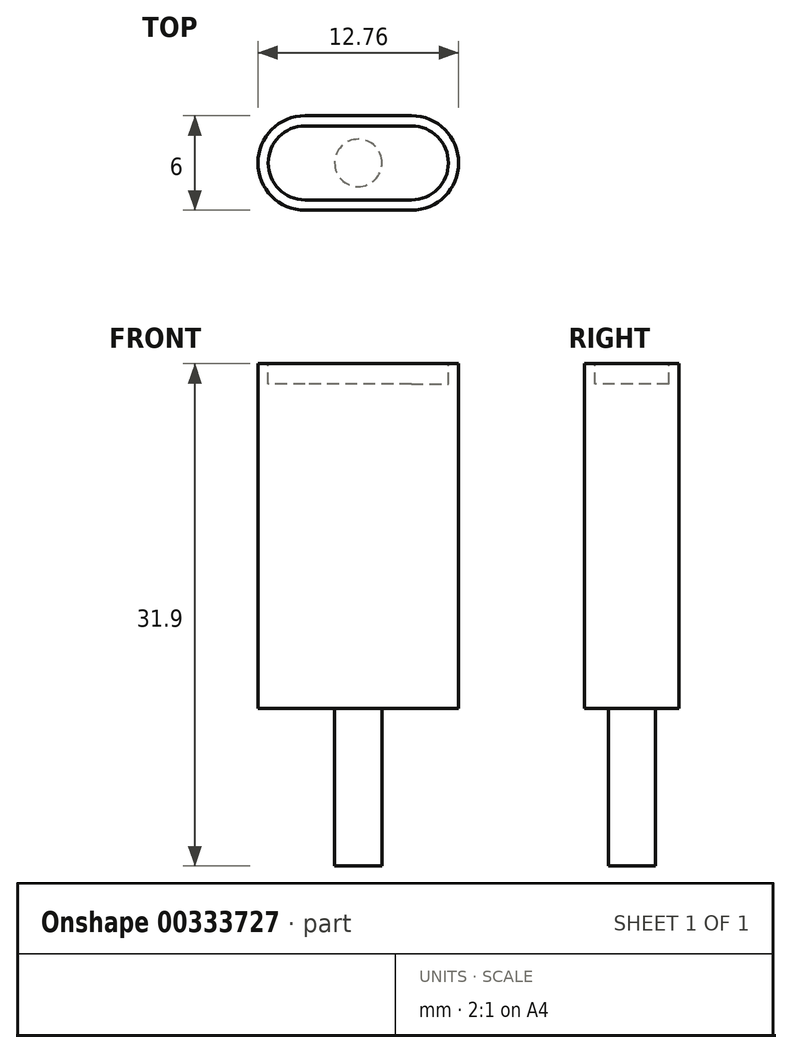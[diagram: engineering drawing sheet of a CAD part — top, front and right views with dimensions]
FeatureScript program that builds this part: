
annotation { "Feature Type Name" : "Feature", "Feature Type Description" : "" }
export const myFeature = defineFeature(function(context is Context, id is Id, definition is map)
    precondition{}
    {
        {
            var Q0;
            Q0=qCreatedBy(makeId("Top.planeOp"),FACE);
            var sketch = newSketch(context, id + "F0", { "sketchPlane" : qUnion([Q0])});
            skLineSegment(sketch, "E0.bottom", {"start": v(6.38, 3) * mm, "end": v(-6.38, 3) * mm});
            skLineSegment(sketch, "E0.top", {"start": v(6.37, -3) * mm, "end": v(-6.38, -3) * mm});
            skLineSegment(sketch, "E0.left", {"start": v(6.38, 3) * mm, "end": v(6.37, -3) * mm});
            skLineSegment(sketch, "E0.right", {"start": v(-6.38, 3) * mm, "end": v(-6.38, -3) * mm});
            skPoint(sketch, "E0.middle", {"position": v(0, 0) * mm});
            skSolve(sketch);
        }
        {
            var Q0;
            Q0=makeQuery(id+"F0.imprint","IMPRINT",FACE,{"disambiguationData":[TD([[makeQuery(id+"F0.imprint","IMPRINT",EDGE,{"derivedFrom":sQuery(id+"F0.wireOp",EDGE,"E0.bottom")}),1.0]])]});
            extrude(context, id + "F1", {"entities" : qUnion([Q0]), "depth" : 21.9 * mm});
        }
        {
            var Q0;
            Q0=makeQuery(id+"F1.opExtrude","SWEPT_EDGE",EDGE,{"disambiguationData":[OSD([sQuery(id+"F0.wireOp",EDGE,"E0.top"),sQuery(id+"F0.wireOp",EDGE,"E0.right")])]});
            var Q1;
            Q1=makeQuery(id+"F1.opExtrude","SWEPT_EDGE",EDGE,{"disambiguationData":[OSD([sQuery(id+"F0.wireOp",EDGE,"E0.bottom"),sQuery(id+"F0.wireOp",EDGE,"E0.right")])]});
            var Q2;
            Q2=makeQuery(id+"F1.opExtrude","SWEPT_EDGE",EDGE,{"disambiguationData":[OSD([sQuery(id+"F0.wireOp",EDGE,"E0.top"),sQuery(id+"F0.wireOp",EDGE,"E0.left")])]});
            var Q3;
            Q3=makeQuery(id+"F1.opExtrude","SWEPT_EDGE",EDGE,{"disambiguationData":[OSD([sQuery(id+"F0.wireOp",EDGE,"E0.bottom"),sQuery(id+"F0.wireOp",EDGE,"E0.left")])]});
            fillet(context, id + "F2", {"entities" : qUnion([Q0, Q1, Q2, Q3]), "radius" : 3 * mm, "tangentPropagation" : true, "allowEdgeOverflow" : false});
        }
        {
            var Q0;
            Q0=makeQuery(id+"F1.opExtrude","CAP_FACE",FACE,{"disambiguationData":[OSD([sQuery(id+"F0.wireOp",EDGE,"E0.bottom"),sQuery(id+"F0.wireOp",EDGE,"E0.top"),sQuery(id+"F0.wireOp",EDGE,"E0.left"),sQuery(id+"F0.wireOp",EDGE,"E0.right")])],"isStart":true});
            var sketch = newSketch(context, id + "F3", { "sketchPlane" : qUnion([Q0])});
            skCircle(sketch, "E1", {"center": v(0, 0) * mm, "radius": 1.5 * mm});
            skSolve(sketch);
        }
        {
            var Q0;
            Q0=makeQuery(id+"F3.imprint","IMPRINT",FACE,{"disambiguationData":[TD([[makeQuery(id+"F3.imprint","IMPRINT",EDGE,{"derivedFrom":sQuery(id+"F3.wireOp",EDGE,"E1")}),1.0]])]});
            extrude(context, id + "F4", {"entities" : qUnion([Q0]), "operationType" : NewBodyOperationType.ADD, "depth" : 10 * mm});
        }
        {
            var Q0;
            Q0=makeQuery(id+"F1.opExtrude","CAP_FACE",FACE,{"disambiguationData":[OSD([sQuery(id+"F0.wireOp",EDGE,"E0.bottom"),sQuery(id+"F0.wireOp",EDGE,"E0.top"),sQuery(id+"F0.wireOp",EDGE,"E0.left"),sQuery(id+"F0.wireOp",EDGE,"E0.right")])],"isStart":false});
            var sketch = newSketch(context, id + "F5", { "sketchPlane" : qUnion([Q0])});
            skLineSegment(sketch, "E2.0.0", {"start": v(-3.38, -3) * mm, "end": v(3.37, -3) * mm});
            skArc(sketch, "E2.0.1", {"start": v(3.37, -3) * mm, "mid": v(6.38, 0) * mm, "end": v(3.38, 3) * mm});
            skLineSegment(sketch, "E2.0.2", {"start": v(3.37, 3) * mm, "end": v(-3.38, 3) * mm});
            skArc(sketch, "E2.0.3", {"start": v(-3.38, 3) * mm, "mid": v(-6.38, 0) * mm, "end": v(-3.38, -3) * mm});
            skArc(sketch, "E3.0", {"start": v(-3.38, 2.35) * mm, "mid": v(-5.73, 0) * mm, "end": v(-3.38, -2.35) * mm});
            skLineSegment(sketch, "E3.1", {"start": v(3.37, 2.35) * mm, "end": v(-3.38, 2.35) * mm});
            skArc(sketch, "E3.2", {"start": v(3.38, -2.35) * mm, "mid": v(5.72, 0) * mm, "end": v(3.37, 2.35) * mm});
            skLineSegment(sketch, "E3.3", {"start": v(-3.38, -2.35) * mm, "end": v(3.37, -2.35) * mm});
            skSolve(sketch);
        }
        {
            var Q0;
            Q0=makeQuery(id+"F5.imprint","IMPRINT",FACE,{"disambiguationData":[TD([[makeQuery(id+"F5.imprint","IMPRINT",EDGE,{"derivedFrom":sQuery(id+"F5.wireOp",EDGE,"E3.0")}),1.0]])]});
            extrude(context, id + "F6", {"entities" : qUnion([Q0]), "operationType" : NewBodyOperationType.REMOVE, "oppositeDirection" : true, "depth" : 1.3 * mm});
        }
    });
